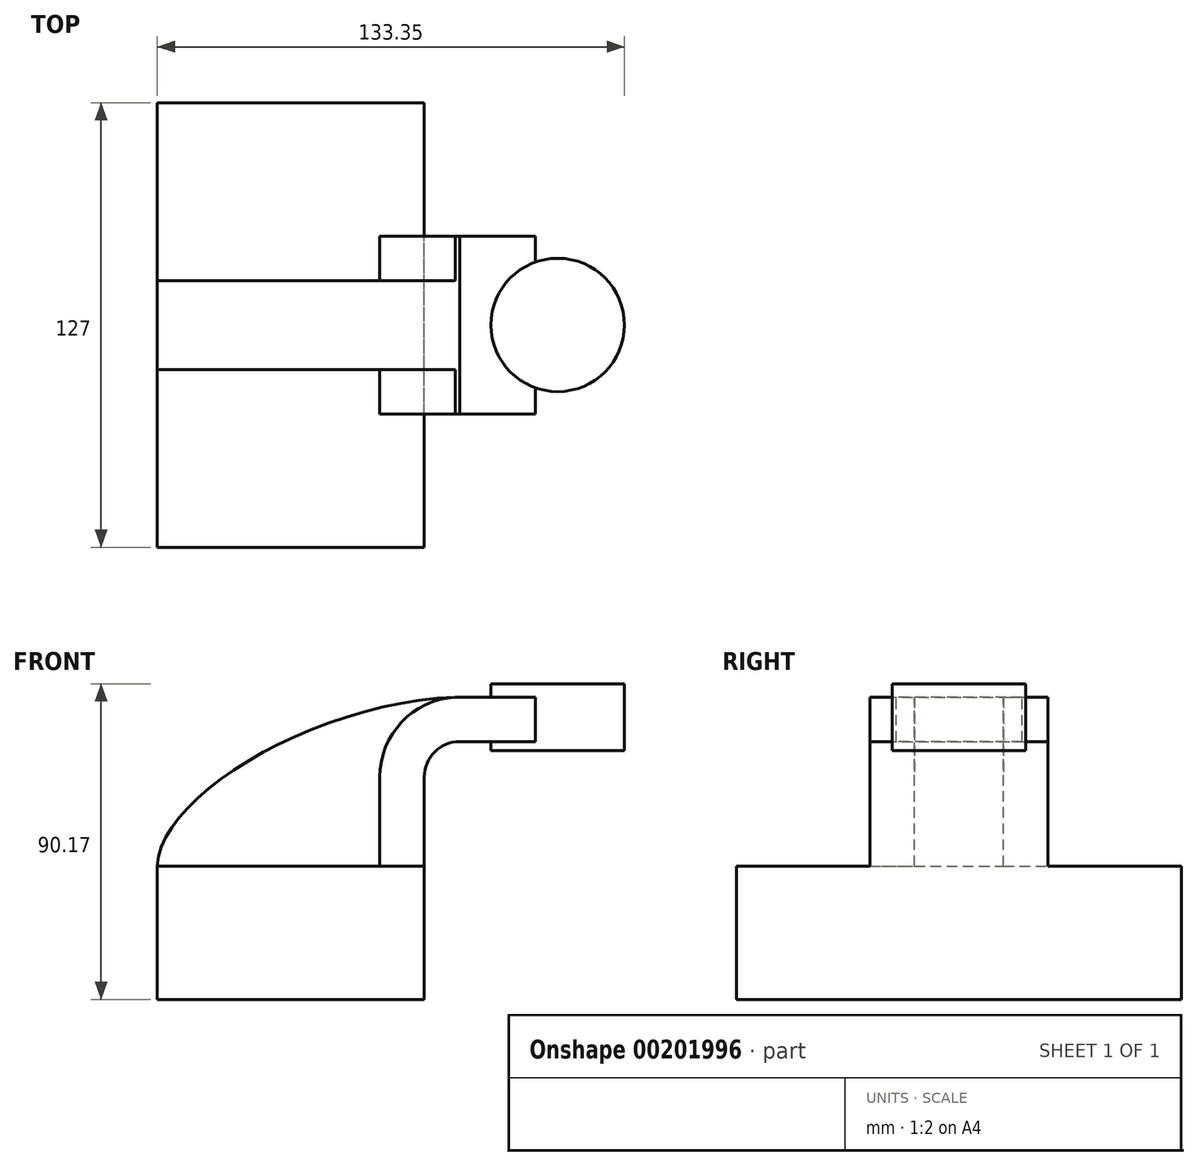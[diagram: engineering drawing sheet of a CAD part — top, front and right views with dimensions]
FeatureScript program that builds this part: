
annotation { "Feature Type Name" : "Feature", "Feature Type Description" : "" }
export const myFeature = defineFeature(function(context is Context, id is Id, definition is map)
    precondition{}
    {
        {
            var Q0;
            Q0=qCreatedBy(makeId("Front.planeOp"),FACE);
            var sketch = newSketch(context, id + "F0", { "sketchPlane" : qUnion([Q0])});
            skLineSegment(sketch, "E0.bottom", {"start": v(-38.1, 19.05) * mm, "end": v(38.1, 19.05) * mm});
            skLineSegment(sketch, "E0.top", {"start": v(-38.1, -19.05) * mm, "end": v(38.1, -19.05) * mm});
            skLineSegment(sketch, "E0.left", {"start": v(-38.1, 19.05) * mm, "end": v(-38.1, -19.05) * mm});
            skLineSegment(sketch, "E0.right", {"start": v(38.1, 19.05) * mm, "end": v(38.1, -19.05) * mm});
            skPoint(sketch, "E0.middle", {"position": v(0, 0) * mm});
            skLineSegment(sketch, "E1.bottom", {"start": v(57.15, 71.12) * mm, "end": v(95.25, 71.12) * mm});
            skLineSegment(sketch, "E1.top", {"start": v(57.15, 52.07) * mm, "end": v(95.25, 52.07) * mm});
            skLineSegment(sketch, "E1.left", {"start": v(57.15, 71.12) * mm, "end": v(57.15, 52.07) * mm});
            skLineSegment(sketch, "E1.right", {"start": v(95.25, 71.12) * mm, "end": v(95.25, 52.07) * mm});
            skPoint(sketch, "E1.middle", {"position": v(76.2, 61.6) * mm});
            skLineSegment(sketch, "E2", {"start": v(38.1, 19.05) * mm, "end": v(38.1, 44.45) * mm});
            skArc(sketch, "E3", {"start": v(38.1, 44.45) * mm, "mid": v(41.08, 51.63) * mm, "end": v(48.26, 54.61) * mm});
            skLineSegment(sketch, "E4", {"start": v(48.26, 54.6) * mm, "end": v(57.15, 54.61) * mm});
            skLineSegment(sketch, "E5.0", {"start": v(48.26, 67.31) * mm, "end": v(57.15, 67.31) * mm});
            skArc(sketch, "E5.1", {"start": v(25.4, 44.45) * mm, "mid": v(32.1, 60.61) * mm, "end": v(48.26, 67.31) * mm});
            skLineSegment(sketch, "E5.2", {"start": v(25.4, 19.05) * mm, "end": v(25.4, 44.45) * mm});
            skFitSpline(sketch, "E6", {"points": [v(-38.1, 19.05) * mm, v(48.26, 67.31) * mm], "startDerivative": vector(2.18, 61.6) * mm, "endDerivative": vector(119.77, 2.57) * mm});
            skLineSegment(sketch, "E7", {"start": v(76.2, 71.12) * mm, "end": v(76.2, 52.07) * mm});
            skLineSegment(sketch, "E8", {"start": v(57.15, 54.61) * mm, "end": v(69.85, 54.61) * mm});
            skLineSegment(sketch, "E9", {"start": v(69.85, 54.61) * mm, "end": v(69.85, 67.31) * mm});
            skLineSegment(sketch, "E10", {"start": v(69.85, 67.31) * mm, "end": v(57.15, 67.31) * mm});
            skSolve(sketch);
        }
        {
            var Q0;
            Q0=makeQuery(id+"F0.imprint","IMPRINT",FACE,{"disambiguationData":[TD([[makeQuery(id+"F0.imprint","IMPRINT",EDGE,{"derivedFrom":sQuery(id+"F0.wireOp",EDGE,"E0.top")}),1.0]])]});
            extrude(context, id + "F1", {"entities" : qUnion([Q0]), "endBound" : BoundingType.SYMMETRIC, "depth" : 127 * mm});
        }
        {
            var Q0;
            {var subQ0=sQuery(id+"F0.wireOp",EDGE,"E2");Q0=makeQuery(id+"F0.imprint","IMPRINT",FACE,{"disambiguationData":[TD([[makeQuery(id+"F0.imprint","IMPRINT",EDGE,{"derivedFrom":subQ0}),1.0]])]});}
            var Q1;
            {var subQ0=sQuery(id+"F0.wireOp",EDGE,"E8");Q1=makeQuery(id+"F0.imprint","IMPRINT",FACE,{"disambiguationData":[TD([[makeQuery(id+"F0.imprint","IMPRINT",EDGE,{"derivedFrom":subQ0}),1.0]])]});}
            extrude(context, id + "F2", {"entities" : qUnion([Q0, Q1]), "operationType" : NewBodyOperationType.ADD, "endBound" : BoundingType.SYMMETRIC, "depth" : 50.8 * mm});
        }
        {
            var Q0;
            {var subQ3=sQuery(id+"F0.wireOp",EDGE,"E5.2");Q0=makeQuery(id+"F0.imprint","IMPRINT",FACE,{"disambiguationData":[TD([[makeQuery(id+"F0.imprint","IMPRINT",EDGE,{"derivedFrom":subQ3}),1.0]])]});}
            extrude(context, id + "F3", {"entities" : qUnion([Q0]), "operationType" : NewBodyOperationType.ADD, "endBound" : BoundingType.SYMMETRIC, "depth" : 25.4 * mm});
        }
        {
            var Q0;
            {var subQ3=sQuery(id+"F0.wireOp",EDGE,"E1.bottom");Q0=makeQuery(id+"F0.imprint","IMPRINT",FACE,{"disambiguationData":[TD([[makeQuery(id+"F0.imprint","IMPRINT",EDGE,{"derivedFrom":subQ3}),-1.0]])]});}
            var Q1;
            Q1=sQuery(id+"F0.wireOp",EDGE,"E7");
            revolve(context, id + "F4", {"operationType" : NewBodyOperationType.ADD, "entities" : qUnion([Q0]), "axis" : qUnion([Q1]), "revolveType" : RevolveType.FULL});
        }
    });
